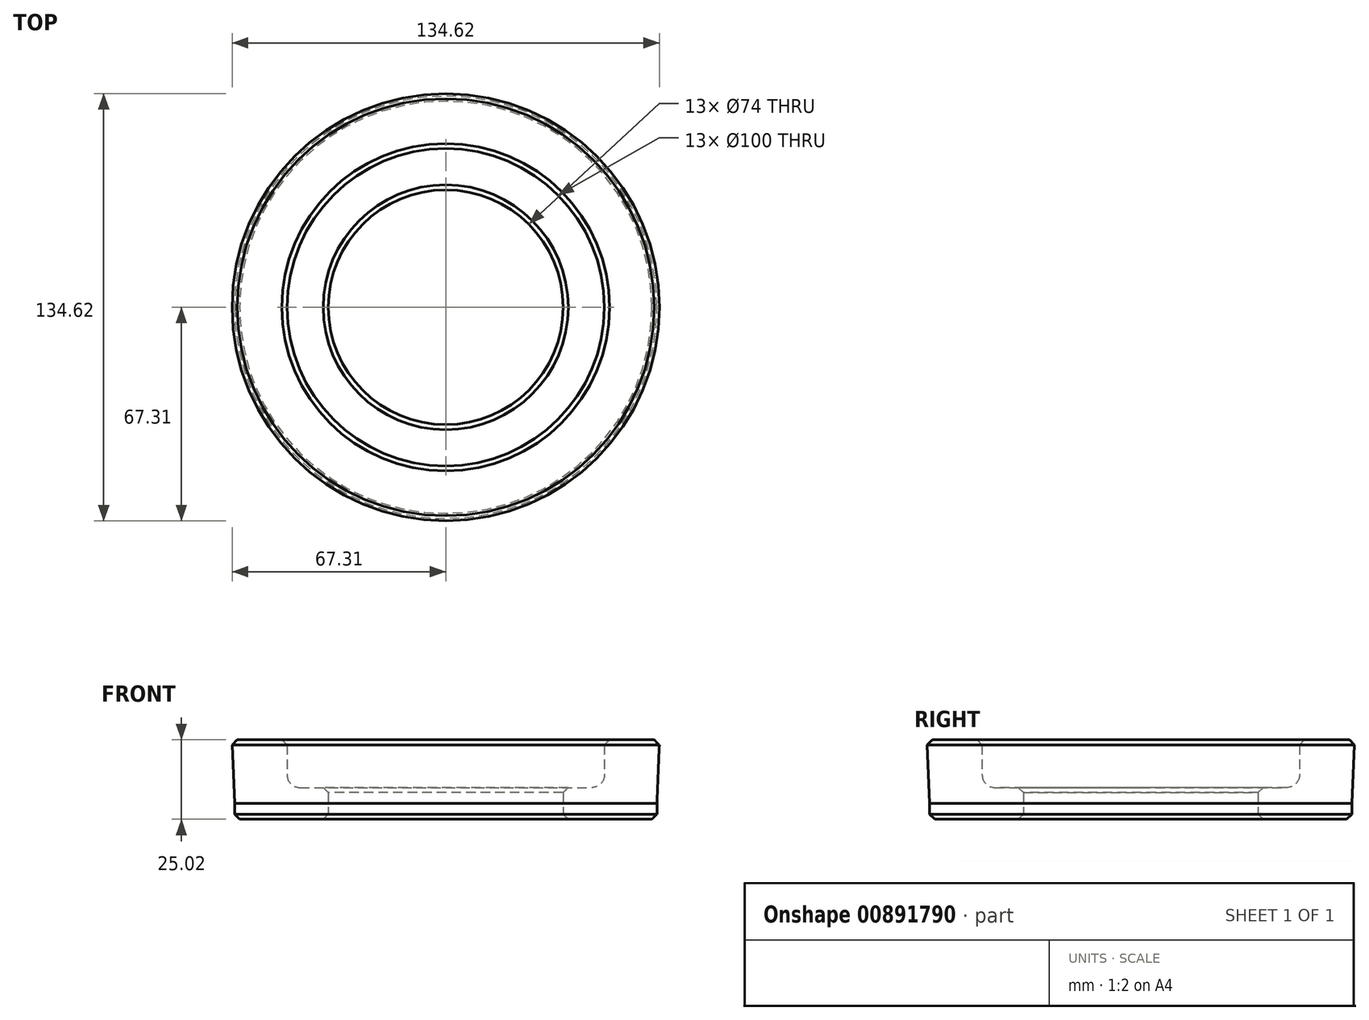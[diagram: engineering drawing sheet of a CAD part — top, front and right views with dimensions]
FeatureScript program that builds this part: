
annotation { "Feature Type Name" : "Feature", "Feature Type Description" : "" }
export const myFeature = defineFeature(function(context is Context, id is Id, definition is map)
    precondition{}
    {
        {
            var Q0;
            Q0=qCreatedBy(makeId("Front.planeOp"),FACE);
            var sketch = newSketch(context, id + "F0", { "sketchPlane" : qUnion([Q0])});
            skLineSegment(sketch, "E0", {"start": v(0, 0) * mm, "end": v(0, 61.52) * mm, "construction": true});
            skLineSegment(sketch, "E1.right", {"start": v(-66.54, 5) * mm, "end": v(-66.54, 0) * mm});
            skLineSegment(sketch, "E2.right", {"start": v(-66.54, 5) * mm, "end": v(-66.54, 5) * mm});
            skLineSegment(sketch, "E3", {"start": v(-67.38, 25.02) * mm, "end": v(-66.54, 5) * mm});
            skPoint(sketch, "E4.end.orphan", {"position": v(-68, 40) * mm});
            skLineSegment(sketch, "E5.bottom", {"start": v(-66.54, 0) * mm, "end": v(-37, 0) * mm});
            skLineSegment(sketch, "E5.top", {"start": v(-46, 10) * mm, "end": v(-37, 10) * mm});
            skLineSegment(sketch, "E5.left", {"start": v(-66.54, 0) * mm, "end": v(-66.54, 5) * mm});
            skLineSegment(sketch, "E5.right", {"start": v(-37, 0) * mm, "end": v(-37, 10) * mm});
            skLineSegment(sketch, "E6.bottom", {"start": v(-67.38, 25.02) * mm, "end": v(-50, 25.02) * mm});
            skLineSegment(sketch, "E6.top", {"start": v(-66.75, 10) * mm, "end": v(-66.54, 10) * mm});
            skLineSegment(sketch, "E6.right", {"start": v(-50, 25.02) * mm, "end": v(-50, 14) * mm});
            skPoint(sketch, "E7.visualSharp", {"position": v(-50, 10) * mm});
            skArc(sketch, "E7.filletArc", {"start": v(-50, 14) * mm, "mid": v(-48.83, 11.17) * mm, "end": v(-46, 10) * mm});
            skPoint(sketch, "E1.top.start.orphan", {"position": v(-67, 0) * mm});
            skSolve(sketch);
        }
        {
            var Q0;
            {var subQ1=sQuery(id+"F0.wireOp",EDGE,"E5.bottom");Q0=makeQuery(id+"F0.imprint","IMPRINT",FACE,{"disambiguationData":[TD([[makeQuery(id+"F0.imprint","IMPRINT",EDGE,{"derivedFrom":subQ1}),1.0]])]});}
            var Q1;
            Q1=sQuery(id+"F0.wireOp",EDGE,"E0");
            revolve(context, id + "F1", {"surfaceOperationType" : NewSurfaceOperationType.NEW, "entities" : qUnion([Q0]), "axis" : qUnion([Q1]), "revolveType" : RevolveType.FULL});
        }
        {
            var Q0;
            Q0=makeQuery(id+"F1.opRevolve","SWEPT_EDGE",EDGE,{"disambiguationData":[OSD([sQuery(id+"F0.wireOp",EDGE,"E5.top"),sQuery(id+"F0.wireOp",EDGE,"E5.right")])]});
            var Q1;
            Q1=makeQuery(id+"F1.opRevolve","SWEPT_EDGE",EDGE,{"disambiguationData":[OSD([sQuery(id+"F0.wireOp",EDGE,"E5.bottom"),sQuery(id+"F0.wireOp",EDGE,"E5.right")])]});
            var Q2;
            Q2=makeQuery(id+"F1.opRevolve","SWEPT_EDGE",EDGE,{"disambiguationData":[OSD([sQuery(id+"F0.wireOp",EDGE,"E5.bottom"),sQuery(id+"F0.wireOp",EDGE,"E5.left")])]});
            var Q3;
            Q3=makeQuery(id+"F1.opRevolve","SWEPT_FACE",FACE,{"disambiguationData":[OSD([sQuery(id+"F0.wireOp",EDGE,"E6.bottom")])]});
            chamfer(context, id + "F2", {"entities" : qUnion([Q0, Q1, Q2, Q3]), "width" : 1.6 * mm, "tangentPropagation" : true});
        }
    });
